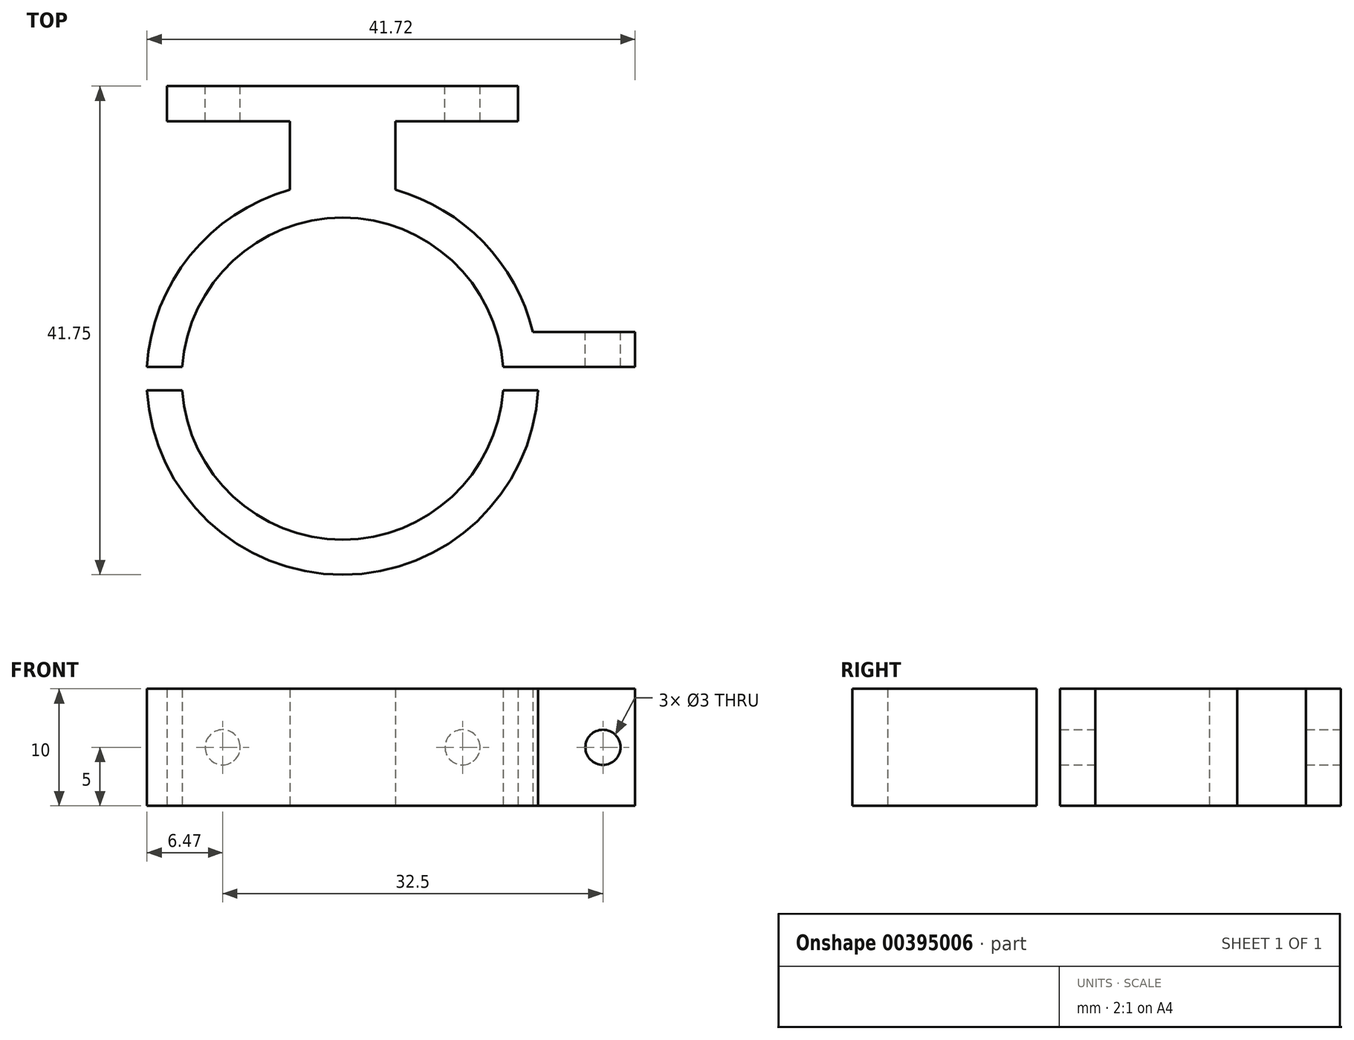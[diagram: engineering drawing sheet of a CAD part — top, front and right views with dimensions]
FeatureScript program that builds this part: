
annotation { "Feature Type Name" : "Feature", "Feature Type Description" : "" }
export const myFeature = defineFeature(function(context is Context, id is Id, definition is map)
    precondition{}
    {
        {
            var Q0;
            Q0=qCreatedBy(makeId("Top.planeOp"),FACE);
            var sketch = newSketch(context, id + "F0", { "sketchPlane" : qUnion([Q0])});
            skCircle(sketch, "E0", {"center": v(0, 0) * mm, "radius": 13.75 * mm});
            skCircle(sketch, "E1.0", {"center": v(0, 0) * mm, "radius": 16.75 * mm});
            skLineSegment(sketch, "E2.bottom", {"start": v(-25, -4) * mm, "end": v(25, -4) * mm});
            skLineSegment(sketch, "E2.top", {"start": v(-25, 4) * mm, "end": v(25, 4) * mm});
            skLineSegment(sketch, "E2.left", {"start": v(-25, -4) * mm, "end": v(-25, 4) * mm});
            skLineSegment(sketch, "E2.right", {"start": v(25, -4) * mm, "end": v(25, 4) * mm});
            skLineSegment(sketch, "E3.bottom", {"start": v(-25, -1) * mm, "end": v(25, -1) * mm});
            skLineSegment(sketch, "E3.top", {"start": v(-25, 1) * mm, "end": v(25, 1) * mm});
            skLineSegment(sketch, "E3.left", {"start": v(-25, -1) * mm, "end": v(-25, 1) * mm});
            skLineSegment(sketch, "E3.right", {"start": v(25, -1) * mm, "end": v(25, 1) * mm});
            skLineSegment(sketch, "E4.bottom", {"start": v(-4.5, -23.5) * mm, "end": v(4.5, -23.5) * mm});
            skLineSegment(sketch, "E4.top", {"start": v(-4.5, 23.5) * mm, "end": v(4.5, 23.5) * mm});
            skLineSegment(sketch, "E4.left", {"start": v(-4.5, -23.5) * mm, "end": v(-4.5, 23.5) * mm});
            skLineSegment(sketch, "E4.right", {"start": v(4.5, -23.5) * mm, "end": v(4.5, 23.5) * mm});
            skLineSegment(sketch, "E5.bottom", {"start": v(15, 22) * mm, "end": v(-15, 22) * mm});
            skLineSegment(sketch, "E5.top", {"start": v(15, 25) * mm, "end": v(-15, 25) * mm});
            skLineSegment(sketch, "E5.left", {"start": v(15, 22) * mm, "end": v(15, 25) * mm});
            skLineSegment(sketch, "E5.right", {"start": v(-15, 22) * mm, "end": v(-15, 25) * mm});
            skPoint(sketch, "E5.middle", {"position": v(0, 23.5) * mm});
            skSolve(sketch);
        }
        {
            var Q0;
            {var subQ5=sQuery(id+"F0.wireOp",EDGE,"E4.top");Q0=makeQuery(id+"F0.imprint","IMPRINT",FACE,{"disambiguationData":[TD([[makeQuery(id+"F0.imprint","IMPRINT",EDGE,{"derivedFrom":subQ5}),1.0]])]});}
            var Q1;
            {var subQ0=sQuery(id+"F0.wireOp",EDGE,"E4.top");Q1=makeQuery(id+"F0.imprint","IMPRINT",FACE,{"disambiguationData":[TD([[makeQuery(id+"F0.imprint","IMPRINT",EDGE,{"derivedFrom":subQ0}),-1.0]])]});}
            var Q2;
            {var subQ0=sQuery(id+"F0.wireOp",EDGE,"E4.right");var subQ1=sQuery(id+"F0.wireOp",EDGE,"E1.0");var subQ2=makeQuery(id+"F0.imprint","INTERSECT",VERTEX,{"disambiguationData":[OD(0.0)],"derivedFrom":[subQ1,subQ0]});Q2=makeQuery(id+"F0.imprint","IMPRINT",FACE,{"disambiguationData":[TD([[makeQuery(id+"F0.imprint","IMPRINT",EDGE,{"disambiguationData":[TD([[subQ2,-1.0]])],"derivedFrom":subQ1}),-1.0]])]});}
            var Q3;
            {var subQ0=sQuery(id+"F0.wireOp",EDGE,"E4.right");var subQ1=sQuery(id+"F0.wireOp",EDGE,"E0");var subQ2=makeQuery(id+"F0.imprint","INTERSECT",VERTEX,{"disambiguationData":[OD(0.0)],"derivedFrom":[subQ1,subQ0]});Q3=makeQuery(id+"F0.imprint","IMPRINT",FACE,{"disambiguationData":[TD([[makeQuery(id+"F0.imprint","IMPRINT",EDGE,{"disambiguationData":[TD([[subQ2,-1.0]])],"derivedFrom":subQ1}),-1.0]])]});}
            var Q4;
            {var subQ0=sQuery(id+"F0.wireOp",EDGE,"E2.top");var subQ1=sQuery(id+"F0.wireOp",EDGE,"E0");var subQ2=makeQuery(id+"F0.imprint","INTERSECT",VERTEX,{"disambiguationData":[OD(0.0)],"derivedFrom":[subQ1,subQ0]});Q4=makeQuery(id+"F0.imprint","IMPRINT",FACE,{"disambiguationData":[TD([[makeQuery(id+"F0.imprint","IMPRINT",EDGE,{"disambiguationData":[TD([[subQ2,-1.0]])],"derivedFrom":subQ1}),-1.0]])]});}
            var Q5;
            {var subQ0=sQuery(id+"F0.wireOp",EDGE,"E4.left");var subQ1=sQuery(id+"F0.wireOp",EDGE,"E0");var subQ2=makeQuery(id+"F0.imprint","INTERSECT",VERTEX,{"disambiguationData":[OD(0.0)],"derivedFrom":[subQ1,subQ0]});Q5=makeQuery(id+"F0.imprint","IMPRINT",FACE,{"disambiguationData":[TD([[makeQuery(id+"F0.imprint","IMPRINT",EDGE,{"disambiguationData":[TD([[subQ2,-1.0]])],"derivedFrom":subQ1}),-1.0]])]});}
            var Q6;
            {var subQ0=sQuery(id+"F0.wireOp",EDGE,"E2.top");var subQ1=sQuery(id+"F0.wireOp",EDGE,"E0");var subQ2=makeQuery(id+"F0.imprint","INTERSECT",VERTEX,{"disambiguationData":[OD(0.0)],"derivedFrom":[subQ1,subQ0]});Q6=makeQuery(id+"F0.imprint","IMPRINT",FACE,{"disambiguationData":[TD([[makeQuery(id+"F0.imprint","IMPRINT",EDGE,{"disambiguationData":[TD([[subQ2,1.0]])],"derivedFrom":subQ1}),-1.0]])]});}
            var Q7;
            {var subQ0=sQuery(id+"F0.wireOp",EDGE,"E2.top");var subQ1=sQuery(id+"F0.wireOp",EDGE,"E1.0");var subQ2=makeQuery(id+"F0.imprint","INTERSECT",VERTEX,{"disambiguationData":[OD(0.0)],"derivedFrom":[subQ1,subQ0]});Q7=makeQuery(id+"F0.imprint","IMPRINT",FACE,{"disambiguationData":[TD([[makeQuery(id+"F0.imprint","IMPRINT",EDGE,{"disambiguationData":[TD([[subQ2,1.0]])],"derivedFrom":subQ1}),-1.0]])]});}
            var Q8;
            {var subQ0=sQuery(id+"F0.wireOp",EDGE,"E2.bottom");var subQ1=sQuery(id+"F0.wireOp",EDGE,"E1.0");var subQ2=makeQuery(id+"F0.imprint","INTERSECT",VERTEX,{"disambiguationData":[OD(1.0)],"derivedFrom":[subQ1,subQ0]});Q8=makeQuery(id+"F0.imprint","IMPRINT",FACE,{"disambiguationData":[TD([[makeQuery(id+"F0.imprint","IMPRINT",EDGE,{"disambiguationData":[TD([[subQ2,-1.0]])],"derivedFrom":subQ1}),-1.0]])]});}
            var Q9;
            {var subQ0=sQuery(id+"F0.wireOp",EDGE,"E2.bottom");var subQ1=sQuery(id+"F0.wireOp",EDGE,"E0");var subQ2=makeQuery(id+"F0.imprint","INTERSECT",VERTEX,{"disambiguationData":[OD(1.0)],"derivedFrom":[subQ1,subQ0]});Q9=makeQuery(id+"F0.imprint","IMPRINT",FACE,{"disambiguationData":[TD([[makeQuery(id+"F0.imprint","IMPRINT",EDGE,{"disambiguationData":[TD([[subQ2,-1.0]])],"derivedFrom":subQ1}),-1.0]])]});}
            var Q10;
            {var subQ0=sQuery(id+"F0.wireOp",EDGE,"E4.right");var subQ1=sQuery(id+"F0.wireOp",EDGE,"E0");var subQ2=makeQuery(id+"F0.imprint","INTERSECT",VERTEX,{"disambiguationData":[OD(1.0)],"derivedFrom":[subQ1,subQ0]});Q10=makeQuery(id+"F0.imprint","IMPRINT",FACE,{"disambiguationData":[TD([[makeQuery(id+"F0.imprint","IMPRINT",EDGE,{"disambiguationData":[TD([[subQ2,-1.0]])],"derivedFrom":subQ1}),-1.0]])]});}
            var Q11;
            {var subQ0=sQuery(id+"F0.wireOp",EDGE,"E2.bottom");var subQ1=sQuery(id+"F0.wireOp",EDGE,"E0");var subQ2=makeQuery(id+"F0.imprint","INTERSECT",VERTEX,{"disambiguationData":[OD(0.0)],"derivedFrom":[subQ1,subQ0]});Q11=makeQuery(id+"F0.imprint","IMPRINT",FACE,{"disambiguationData":[TD([[makeQuery(id+"F0.imprint","IMPRINT",EDGE,{"disambiguationData":[TD([[subQ2,-1.0]])],"derivedFrom":subQ1}),-1.0]])]});}
            var Q12;
            {var subQ0=sQuery(id+"F0.wireOp",EDGE,"E3.bottom");var subQ1=sQuery(id+"F0.wireOp",EDGE,"E0");var subQ2=makeQuery(id+"F0.imprint","INTERSECT",VERTEX,{"disambiguationData":[OD(0.0)],"derivedFrom":[subQ1,subQ0]});Q12=makeQuery(id+"F0.imprint","IMPRINT",FACE,{"disambiguationData":[TD([[makeQuery(id+"F0.imprint","IMPRINT",EDGE,{"disambiguationData":[TD([[subQ2,-1.0]])],"derivedFrom":subQ1}),-1.0]])]});}
            var Q13;
            {var subQ0=sQuery(id+"F0.wireOp",EDGE,"E3.top");var subQ1=sQuery(id+"F0.wireOp",EDGE,"E0");var subQ2=makeQuery(id+"F0.imprint","INTERSECT",VERTEX,{"disambiguationData":[OD(1.0)],"derivedFrom":[subQ1,subQ0]});Q13=makeQuery(id+"F0.imprint","IMPRINT",FACE,{"disambiguationData":[TD([[makeQuery(id+"F0.imprint","IMPRINT",EDGE,{"disambiguationData":[TD([[subQ2,-1.0]])],"derivedFrom":subQ1}),-1.0]])]});}
            var Q14;
            {var subQ0=sQuery(id+"F0.wireOp",EDGE,"E2.top");var subQ1=sQuery(id+"F0.wireOp",EDGE,"E0");var subQ2=makeQuery(id+"F0.imprint","INTERSECT",VERTEX,{"disambiguationData":[OD(1.0)],"derivedFrom":[subQ1,subQ0]});Q14=makeQuery(id+"F0.imprint","IMPRINT",FACE,{"disambiguationData":[TD([[makeQuery(id+"F0.imprint","IMPRINT",EDGE,{"disambiguationData":[TD([[subQ2,-1.0]])],"derivedFrom":subQ1}),-1.0]])]});}
            var Q15;
            {var subQ0=sQuery(id+"F0.wireOp",EDGE,"E4.left");var subQ1=sQuery(id+"F0.wireOp",EDGE,"E0");var subQ2=makeQuery(id+"F0.imprint","INTERSECT",VERTEX,{"disambiguationData":[OD(1.0)],"derivedFrom":[subQ1,subQ0]});Q15=makeQuery(id+"F0.imprint","IMPRINT",FACE,{"disambiguationData":[TD([[makeQuery(id+"F0.imprint","IMPRINT",EDGE,{"disambiguationData":[TD([[subQ2,-1.0]])],"derivedFrom":subQ1}),-1.0]])]});}
            extrude(context, id + "F1", {"entities" : qUnion([Q0, Q1, Q2, Q3, Q4, Q5, Q6, Q7, Q8, Q9, Q10, Q11, Q12, Q13, Q14, Q15]), "depth" : 10 * mm});
        }
        {
            var Q0;
            Q0=makeQuery(id+"F1.opExtrude","SWEPT_FACE",FACE,{"disambiguationData":[OSD([sQuery(id+"F0.wireOp",EDGE,"E5.top")])]});
            cPlane(context, id + "F2", {"entities" : qUnion([Q0]), "cplaneType" : CPlaneType.OFFSET, "offset" : 0 * mm, "width" : 150 * mm, "height" : 150 * mm});
        }
        {
            var Q0;
            Q0=qCreatedBy(id+"F2.planeOp",FACE);
            var sketch = newSketch(context, id + "F3", { "sketchPlane" : qUnion([Q0])});
            skLineSegment(sketch, "E6", {"start": v(0, 0) * mm, "end": v(0, 5) * mm, "construction": true});
            skLineSegment(sketch, "E7", {"start": v(0, 5) * mm, "end": v(-10.25, 5) * mm, "construction": true});
            skCircle(sketch, "E8", {"center": v(-10.25, 5) * mm, "radius": 1.5 * mm});
            skCircle(sketch, "E9.MirrorC", {"center": v(10.25, 5) * mm, "radius": 1.5 * mm});
            skLineSegment(sketch, "E10", {"start": v(-10.25, 5) * mm, "end": v(-22.25, 5) * mm, "construction": true});
            skCircle(sketch, "E11", {"center": v(-22.25, 5) * mm, "radius": 1.5 * mm});
            skSolve(sketch);
        }
        {
            var Q0;
            Q0 = qSketchRegion(id + "F3", true);
            extrude(context, id + "F4", {"entities" : qUnion([Q0]), "operationType" : NewBodyOperationType.REMOVE, "endBound" : BoundingType.UP_TO_NEXT, "oppositeDirection" : true, "depth" : 25 * mm});
        }
        {
            var Q0;
            Q0=makeQuery(id+"F3.imprint","IMPRINT",FACE,{"disambiguationData":[TD([[makeQuery(id+"F3.imprint","IMPRINT",EDGE,{"derivedFrom":sQuery(id+"F3.wireOp",EDGE,"E11")}),1.0]])]});
            extrude(context, id + "F5", {"entities" : qUnion([Q0]), "operationType" : NewBodyOperationType.REMOVE, "endBound" : BoundingType.THROUGH_ALL, "oppositeDirection" : true, "depth" : 25 * mm});
        }
    });
